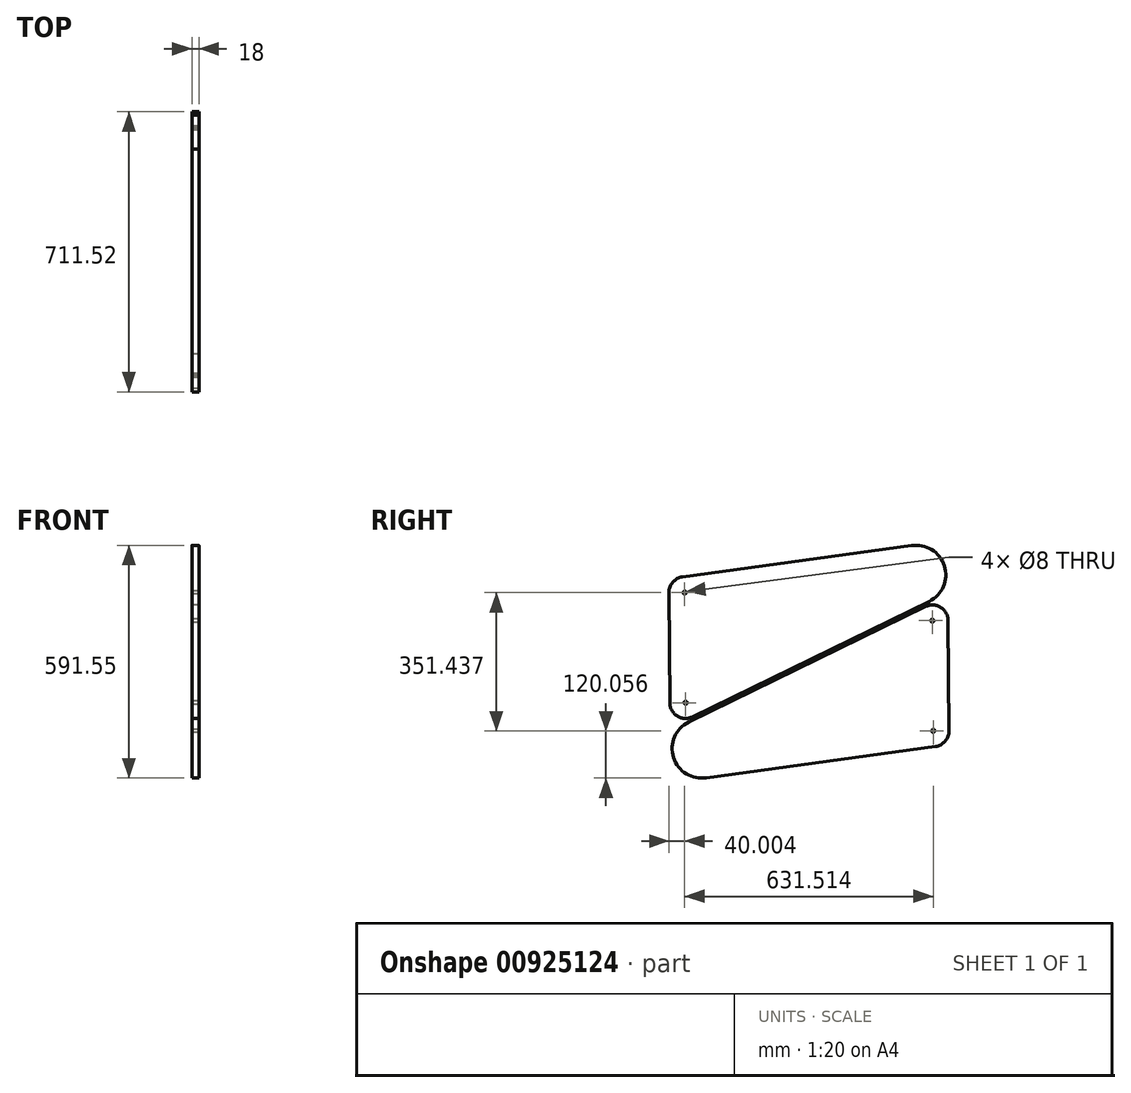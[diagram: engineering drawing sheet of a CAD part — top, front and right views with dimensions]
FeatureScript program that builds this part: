
annotation { "Feature Type Name" : "Feature", "Feature Type Description" : "" }
export const myFeature = defineFeature(function(context is Context, id is Id, definition is map)
    precondition{}
    {
        {
            var Q0;
            Q0=qCreatedBy(makeId("Right.planeOp"),FACE);
            var sketch = newSketch(context, id + "F0", { "sketchPlane" : qUnion([Q0])});
            skLineSegment(sketch, "E0.0", {"start": v(-39.7, -0.12) * mm, "end": v(-42.1, 280.22) * mm});
            skArc(sketch, "E1", {"start": v(619.08, 257.88) * mm, "mid": v(657.63, 348.04) * mm, "end": v(574.04, 399.29) * mm});
            skPoint(sketch, "E2.visualSharp", {"position": v(-42.42, 317) * mm});
            skArc(sketch, "E2.filletArc", {"start": v(-7.52, 319.86) * mm, "mid": v(-32.24, 306.52) * mm, "end": v(-42.1, 280.22) * mm});
            skPoint(sketch, "E3.visualSharp", {"position": v(-39.11, -67.85) * mm});
            skArc(sketch, "E3.filletArc", {"start": v(-39.7, -0.12) * mm, "mid": v(-20.74, -33.8) * mm, "end": v(17.86, -35.72) * mm});
            skLineSegment(sketch, "E4", {"start": v(574.04, 399.29) * mm, "end": v(-7.52, 319.86) * mm});
            skLineSegment(sketch, "E5", {"start": v(619.08, 257.88) * mm, "end": v(17.86, -35.72) * mm});
            skCircle(sketch, "E6", {"center": v(-2.1, 280.22) * mm, "radius": 4 * mm});
            skCircle(sketch, "E7", {"center": v(0.3, 0.22) * mm, "radius": 4 * mm});
            skLineSegment(sketch, "E8", {"start": v(586.17, 400.28) * mm, "end": v(152.67, 400.28) * mm, "construction": true});
            skLineSegment(sketch, "E9.0", {"start": v(667, 209.13) * mm, "end": v(669.4, -71.21) * mm});
            skArc(sketch, "E10", {"start": v(8.22, -48.87) * mm, "mid": v(-30.33, -139.03) * mm, "end": v(53.27, -190.28) * mm});
            skPoint(sketch, "E11.visualSharp", {"position": v(670, -139.72) * mm});
            skArc(sketch, "E11.filletArc", {"start": v(634.82, -110.85) * mm, "mid": v(659.55, -97.51) * mm, "end": v(669.4, -71.21) * mm});
            skPoint(sketch, "E12.visualSharp", {"position": v(666.69, 245.14) * mm});
            skArc(sketch, "E12.filletArc", {"start": v(667, 209.13) * mm, "mid": v(648.04, 242.8) * mm, "end": v(609.45, 244.73) * mm});
            skLineSegment(sketch, "E13", {"start": v(53.27, -190.28) * mm, "end": v(634.82, -110.85) * mm});
            skLineSegment(sketch, "E14", {"start": v(8.22, -48.87) * mm, "end": v(609.45, 244.73) * mm});
            skCircle(sketch, "E15", {"center": v(629.4, -71.21) * mm, "radius": 4 * mm});
            skCircle(sketch, "E16", {"center": v(627, 208.79) * mm, "radius": 4 * mm});
            skLineSegment(sketch, "E17", {"start": v(41.13, -191.27) * mm, "end": v(1450.35, -191.27) * mm, "construction": true});
            skLineSegment(sketch, "E18", {"start": v(-39.7, -0.12) * mm, "end": v(-36.55, -365.74) * mm, "construction": true});
            skSolve(sketch);
        }
        {
            var Q0;
            Q0 = qSketchRegion(id + "F0", true);
            extrude(context, id + "F1", {"entities" : qUnion([Q0]), "depth" : 18 * mm, "offsetDistance" : 25 * mm});
        }
    });
